# Revit family: Vulcan_Cabinet Unit
name_source: partatom
category: Mechanical Equipment
revit_build: Autodesk Revit 2017 (Build: 20160225_1515(x64)
units: mm (PartAtom-declared; Revit-internal decimal feet)

## family parameters
Always vertical = No
Cut with Voids When Loaded = No
OmniClass Number = 23.75.00.00
OmniClass Title = Climate Control (HVAC)
Part Type = Normal
Room Calculation Point = No
Round Connector Dimension = Use Diameter
Shared = No
Work Plane-Based = Yes

## types (1)
- Cabinet Unit
    Altitude = 0"
    Ambient Air Temp = 0 °F
    Apparent load = 0 VA
    Base Height = 3.75"
    Brand = 1
    CTRL_ Condenser Support Height = 21.02"
    CTRL_ Economiser Middle Support Width = 5.3"
    CTRL_Cente of Convenience Outlet_X Dist. = 2.17"
    CTRL_Cente of Convenience Outlet_Y Dist. = 10.11"
    CTRL_Cente of Drain_X Dist. = 38.75"
    CTRL_Cente of Drain_Y Dist. = 2.28"
    CTRL_Cente of Gas Inlet_X Dist. = 81.44"
    CTRL_Cente of Gas Inlet_Y Dist. = 6.87"
    CTRL_Cente of Power Entry (Bottom)_X Dist. = 129.24"
    CTRL_Cente of Power Entry (Bottom)_Y Dist. = 8.5"
    CTRL_Cente of Power Entry_X Dist. = 117.51"
    CTRL_Cente of Power Entry_Y Dist. = 7.44"
    CTRL_Coil Guard = Yes
    CTRL_Coil Guard_27.5-35 tons = Yes
    CTRL_Condenser Fan Diameter = 30.88"
    CTRL_Condenser Fan Height = 5.64"
    CTRL_Convenience Outlet Dia. = 0.22"
    CTRL_Disconnect Switch Height = 5"
    CTRL_Disconnect Switch Width = 10"
    CTRL_Disconnect Switch_X Dist. = 4.04"
    CTRL_Disconnect Switch_Y Dist. = 11.62"
    CTRL_Electrical Entry Diameter = 0.22"
    CTRL_Evaporator Side Support = 6.99"
    CTRL_Exhaust Flue Hood Visibility = No
    CTRL_Exhaust Hood Location = 3"
    CTRL_Fan Inset from Front = 25"
    CTRL_Fan Inset from Right = 26.02"
    CTRL_Fan Spacing _Y = 20.25"
    CTRL_Fan Spacing_X = 20"
    CTRL_Flue Gas_X Distance = 105.79"
    CTRL_Flue Gas_Y Distance = 22.51"
    CTRL_Gas Connection Diameter (ID) = 0.65"
    CTRL_Gas Inlet Description = *Not Applicable*
    CTRL_Gas Inlet Pipe Visibility = No
    CTRL_Gas Inlet_X Distance from Left = 81.44"
    CTRL_Gas Inlet_Y Distance from Bottom = 6.87"
    CTRL_Hail Guard = No
    CTRL_Panel Thickness = 0.5"
    CTRL_Panel Thickness (Condenser Section) = 0.39"
    CTRL_Power Entry Diameter = 3"
    CTRL_Rail-1_From Left = 30.73"
    CTRL_Rail-2_From Left = 72.32"
    CTRL_Rail-3_From Left = 113.9"
    CTRL_Rail-4_From Left = 135.75"
    CTRL_Return Air Front Inset = 7.09"
    CTRL_Return Air Left Inset = 6.99"
    CTRL_Right Side Support Width = 6.39"
    CTRL_Segment 5_27.5-35 tons = Yes
    CTRL_Segment 5_40-50 tons = No
    CTRL_Supply Air Front Inset = 16.88"
    CTRL_Supply Air Left Inset = 82.99"
    CTRL_Top Bars = 0.74"
    CTRL_Top Offset = 0.98"
    Cabinet Material = Tan
    Clearance Back = 96"
    Clearance Bottom = 0"
    Clearance Front = 90"
    Clearance Left = 60"
    Clearance Right = 96"
    Clearance Top = 120"
    Coil Material = Dark Gray
    Condensate Drain Diameter = 1"
    Cooling & Heating Configuration = 1
    Default Elevation = 48"
    Efficiency = Standard Capacity, Standard Efficiency
    Electric Heat TMBH = 0.0 Btu/h
    Entering Air Temp DB = 0 °F
    Entering Air Temp WB = 0 °F
    Exhaust Configuration = 1
    Exhaust Hood Visibility = Yes
    FLA = 0 A
    Frequency = 60 Hz
    Gas Connection Diameter = 0.75"
    Gas Heat MBH Input = 0.0 Btu/h
    Gas Heat MBH Output = 0.0 Btu/h
    Guards Configuration = 1
    Heating EAT = 0 °F
    Heating LAT = 0 °F
    Louver Material = Louver Panel
    MCA = 0 A
    MDEF/Max CB = 0 A
    MOP = 0 A
    Manufacturer = Johnson Controls, Inc.
    Model = York_AC_Package_(27.5 ton)_Cooling Only
    Nominal Cooling Capacity = 27.5 ton
    Number of Poles = 3
    OA Configuration = 2
    OA Hood Visibility = Yes
    Power Factor = 1
    Refrigerant Used = R-410A
    Return Air Configuration = 1
    Return Air Height = 75.81"
    Return Air Width = 22.50"
    Return/Exhaust ESP = 0.00 in-wg
    SMBH Cooling = 0.0 ton
    Segment-1 = 31.56"
    Segment-2 = 31.35"
    Segment-3 = 36.69"
    Segment-4 = 19"
    Segment-5 = 80.66"
    Supply Air Configuration = 1
    Supply Air Height = 66.00"
    Supply Air Width = 26.50"
    Supply ESP = 0.00 in-wg
    Support-1 = 6.7"
    Support-2 = 3.3"
    Support-3 = 2"
    Support-4 = 2"
    Support-5 = 4.35"
    TMBH Cooling = 0.0 ton
    Tonnage = 1
    URL = www.johnsoncontrols.com
    Unit Base Length = 180"
    Unit Height = 70"
    Unit Leaving Air Temp DB = 0 °F
    Unit Leaving Air Temp WB = 0 °F
    Unit Length = 217.61"
    Unit Width = 90"
    Voltage = 230 V
    Weight = 0.00 lb

## geometry (parser evidence)
native form markers: Sweep x29
no freeform markers — native parametric forms only
